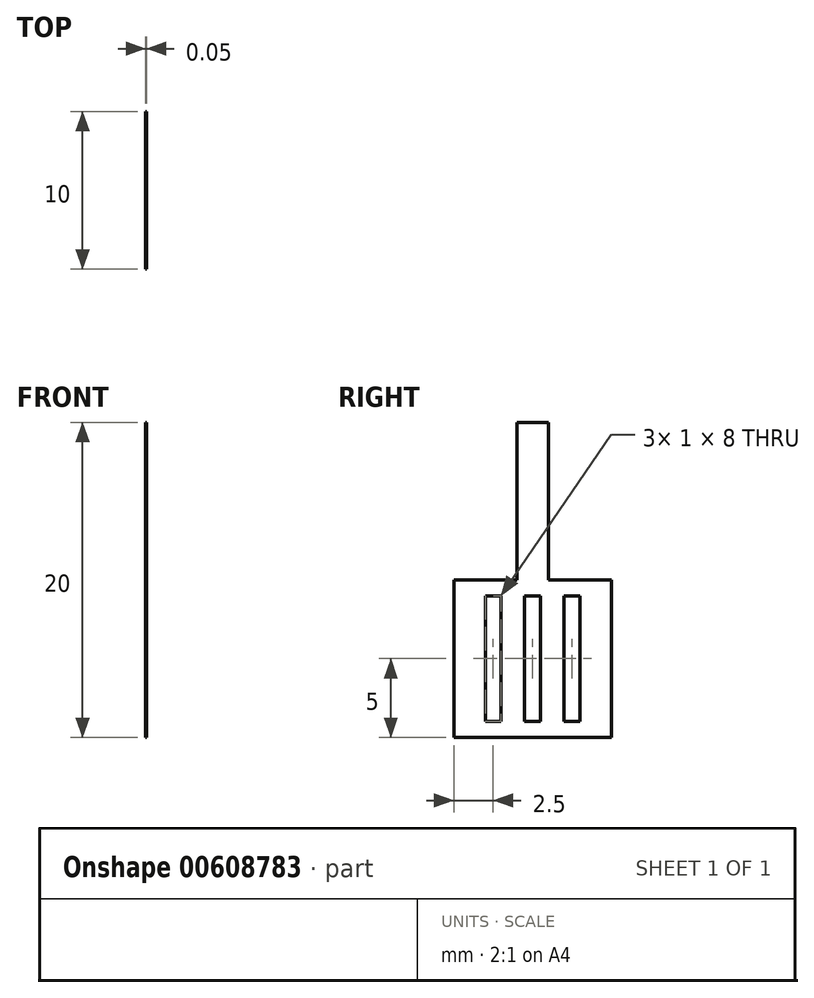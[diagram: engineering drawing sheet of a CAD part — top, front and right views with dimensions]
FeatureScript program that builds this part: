
annotation { "Feature Type Name" : "Feature", "Feature Type Description" : "" }
export const myFeature = defineFeature(function(context is Context, id is Id, definition is map)
    precondition{}
    {
        {
            var Q0;
            Q0=qCreatedBy(makeId("Right.planeOp"),FACE);
            var sketch = newSketch(context, id + "F0", { "sketchPlane" : qUnion([Q0])});
            skLineSegment(sketch, "E0.bottom", {"start": v(0, 0) * mm, "end": v(10, 0) * mm});
            skLineSegment(sketch, "E0.top", {"start": v(0, 10) * mm, "end": v(4, 10) * mm});
            skLineSegment(sketch, "E0.left", {"start": v(0, 0) * mm, "end": v(0, 10) * mm});
            skLineSegment(sketch, "E0.right", {"start": v(10, 0) * mm, "end": v(10, 10) * mm});
            skLineSegment(sketch, "E1.0", {"start": v(6, 10) * mm, "end": v(6, 20) * mm});
            skLineSegment(sketch, "E2.0", {"start": v(4, 10) * mm, "end": v(4, 20) * mm});
            skLineSegment(sketch, "E3", {"start": v(4, 20) * mm, "end": v(6, 20) * mm});
            skLineSegment(sketch, "E4.trimOffspring", {"start": v(6, 10) * mm, "end": v(10, 10) * mm});
            skLineSegment(sketch, "E5", {"start": v(0, 10) * mm, "end": v(0, 9) * mm});
            skLineSegment(sketch, "E6", {"start": v(0, 0) * mm, "end": v(0, 1) * mm});
            skLineSegment(sketch, "E7", {"start": v(2, 9) * mm, "end": v(3, 9) * mm});
            skLineSegment(sketch, "E8", {"start": v(2, 1) * mm, "end": v(3, 1) * mm});
            skLineSegment(sketch, "E9.0", {"start": v(2, 1) * mm, "end": v(2, 9) * mm});
            skLineSegment(sketch, "E10.0", {"start": v(8, 1) * mm, "end": v(8, 9) * mm});
            skLineSegment(sketch, "E11.0", {"start": v(3, 1) * mm, "end": v(3, 9) * mm});
            skLineSegment(sketch, "E12.0", {"start": v(4.5, 1) * mm, "end": v(4.5, 9) * mm});
            skLineSegment(sketch, "E13.0", {"start": v(5.5, 1) * mm, "end": v(5.5, 9) * mm});
            skLineSegment(sketch, "E14.0", {"start": v(7, 1) * mm, "end": v(7, 9) * mm});
            skLineSegment(sketch, "E15.trimOffspring", {"start": v(4.5, 9) * mm, "end": v(5.5, 9) * mm});
            skLineSegment(sketch, "E16.trimOffspring", {"start": v(7, 9) * mm, "end": v(8, 9) * mm});
            skLineSegment(sketch, "E17.trimOffspring", {"start": v(4.5, 1) * mm, "end": v(5.5, 1) * mm});
            skLineSegment(sketch, "E18.trimOffspring", {"start": v(7, 1) * mm, "end": v(8, 1) * mm});
            skSolve(sketch);
        }
        {
            var Q0;
            Q0=makeQuery(id+"F0.imprint","IMPRINT",FACE,{"disambiguationData":[TD([[makeQuery(id+"F0.imprint","IMPRINT",EDGE,{"derivedFrom":sQuery(id+"F0.wireOp",EDGE,"E0.bottom")}),1.0]])]});
            extrude(context, id + "F1", {"entities" : qUnion([Q0]), "depth" : 0.05 * mm, "offsetDistance" : 25 * mm});
        }
    });
